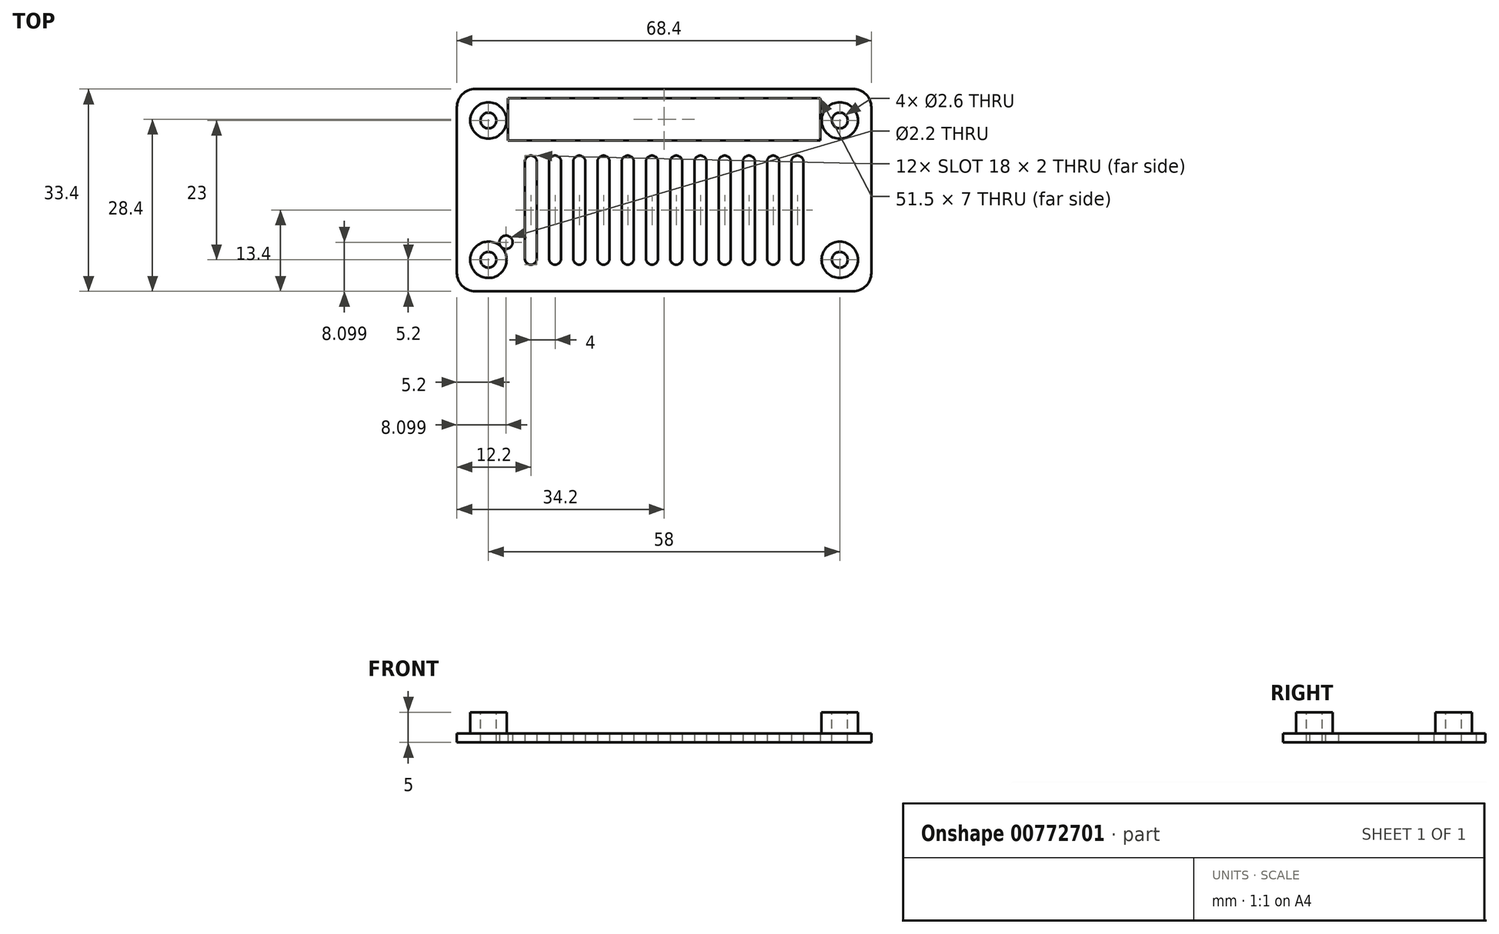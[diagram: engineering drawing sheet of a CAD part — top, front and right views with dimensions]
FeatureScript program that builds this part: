
annotation { "Feature Type Name" : "Feature", "Feature Type Description" : "" }
export const myFeature = defineFeature(function(context is Context, id is Id, definition is map)
    precondition{}
    {
        {
            var Q0;
            Q0=qCreatedBy(makeId("Top.planeOp"),FACE);
            var sketch = newSketch(context, id + "F0", { "sketchPlane" : qUnion([Q0])});
            skLineSegment(sketch, "E0.bottom", {"start": v(-29.5, 15) * mm, "end": v(29.5, 15) * mm, "construction": true});
            skLineSegment(sketch, "E0.top", {"start": v(-29.5, -15) * mm, "end": v(29.5, -15) * mm, "construction": true});
            skLineSegment(sketch, "E0.left", {"start": v(-32.5, 12) * mm, "end": v(-32.5, -12) * mm, "construction": true});
            skLineSegment(sketch, "E0.right", {"start": v(32.5, 12) * mm, "end": v(32.5, -12) * mm, "construction": true});
            skPoint(sketch, "E1.visualSharp", {"position": v(-32.5, 15) * mm});
            skArc(sketch, "E1.filletArc", {"start": v(-29.5, 15) * mm, "mid": v(-31.62, 14.12) * mm, "end": v(-32.5, 12) * mm, "construction": true});
            skPoint(sketch, "E2.visualSharp", {"position": v(32.5, 15) * mm});
            skArc(sketch, "E2.filletArc", {"start": v(32.5, 12) * mm, "mid": v(31.62, 14.12) * mm, "end": v(29.5, 15) * mm, "construction": true});
            skPoint(sketch, "E3.visualSharp", {"position": v(32.5, -15) * mm});
            skArc(sketch, "E3.filletArc", {"start": v(29.5, -15) * mm, "mid": v(31.62, -14.12) * mm, "end": v(32.5, -12) * mm, "construction": true});
            skPoint(sketch, "E4.visualSharp", {"position": v(-32.5, -15) * mm});
            skArc(sketch, "E4.filletArc", {"start": v(-32.5, -12) * mm, "mid": v(-31.62, -14.12) * mm, "end": v(-29.5, -15) * mm, "construction": true});
            skCircle(sketch, "E5", {"center": v(-29, 11.5) * mm, "radius": 3 * mm});
            skCircle(sketch, "E6.0.1.0", {"center": v(-29, -11.5) * mm, "radius": 3 * mm});
            skCircle(sketch, "E6.1.0.0", {"center": v(29, 11.5) * mm, "radius": 3 * mm});
            skCircle(sketch, "E6.1.1.0", {"center": v(29, -11.5) * mm, "radius": 3 * mm});
            skLineSegment(sketch, "E6.direction1", {"start": v(-29, 11.5) * mm, "end": v(29, 11.5) * mm, "construction": true});
            skLineSegment(sketch, "E6.direction2", {"start": v(-29, 11.5) * mm, "end": v(-29, -11.5) * mm, "construction": true});
            skCircle(sketch, "E7", {"center": v(-29, 11.5) * mm, "radius": 1.3 * mm});
            skCircle(sketch, "E8.0.1.0", {"center": v(-29, -11.5) * mm, "radius": 1.3 * mm});
            skCircle(sketch, "E8.1.0.0", {"center": v(29, 11.5) * mm, "radius": 1.3 * mm});
            skCircle(sketch, "E8.1.1.0", {"center": v(29, -11.5) * mm, "radius": 1.3 * mm});
            skLineSegment(sketch, "E9.bottom", {"start": v(-29.7, 15.2) * mm, "end": v(29.7, 15.2) * mm});
            skLineSegment(sketch, "E9.top", {"start": v(-29.7, -15.2) * mm, "end": v(29.7, -15.2) * mm});
            skLineSegment(sketch, "E9.left", {"start": v(-32.7, 12.2) * mm, "end": v(-32.7, -12.2) * mm});
            skLineSegment(sketch, "E9.right", {"start": v(32.7, 12.2) * mm, "end": v(32.7, -12.2) * mm});
            skPoint(sketch, "E10.visualSharp", {"position": v(-32.7, 15.2) * mm});
            skArc(sketch, "E10.filletArc", {"start": v(-29.7, 15.2) * mm, "mid": v(-31.82, 14.32) * mm, "end": v(-32.7, 12.2) * mm});
            skPoint(sketch, "E11.visualSharp", {"position": v(-32.7, -15.2) * mm});
            skArc(sketch, "E11.filletArc", {"start": v(-32.7, -12.2) * mm, "mid": v(-31.82, -14.32) * mm, "end": v(-29.7, -15.2) * mm});
            skPoint(sketch, "E12.visualSharp", {"position": v(32.7, -15.2) * mm});
            skArc(sketch, "E12.filletArc", {"start": v(29.7, -15.2) * mm, "mid": v(31.82, -14.32) * mm, "end": v(32.7, -12.2) * mm});
            skPoint(sketch, "E13.visualSharp", {"position": v(32.7, 15.2) * mm});
            skArc(sketch, "E13.filletArc", {"start": v(32.7, 12.2) * mm, "mid": v(31.82, 14.32) * mm, "end": v(29.7, 15.2) * mm});
            skLineSegment(sketch, "E14.bottom", {"start": v(-31.2, 16.7) * mm, "end": v(31.2, 16.7) * mm});
            skLineSegment(sketch, "E14.top", {"start": v(-31.2, -16.7) * mm, "end": v(31.2, -16.7) * mm});
            skLineSegment(sketch, "E14.left", {"start": v(-34.2, 13.7) * mm, "end": v(-34.2, -13.7) * mm});
            skLineSegment(sketch, "E14.right", {"start": v(34.2, 13.7) * mm, "end": v(34.2, -13.7) * mm});
            skPoint(sketch, "E15.visualSharp", {"position": v(-34.2, 16.7) * mm});
            skArc(sketch, "E15.filletArc", {"start": v(-31.2, 16.7) * mm, "mid": v(-33.32, 15.82) * mm, "end": v(-34.2, 13.7) * mm});
            skPoint(sketch, "E16.visualSharp", {"position": v(-34.2, -16.7) * mm});
            skArc(sketch, "E16.filletArc", {"start": v(-34.2, -13.7) * mm, "mid": v(-33.32, -15.82) * mm, "end": v(-31.2, -16.7) * mm});
            skPoint(sketch, "E17.visualSharp", {"position": v(34.2, -16.7) * mm});
            skArc(sketch, "E17.filletArc", {"start": v(31.2, -16.7) * mm, "mid": v(33.32, -15.82) * mm, "end": v(34.2, -13.7) * mm});
            skPoint(sketch, "E18.visualSharp", {"position": v(34.2, 16.7) * mm});
            skArc(sketch, "E18.filletArc", {"start": v(34.2, 13.7) * mm, "mid": v(33.32, 15.82) * mm, "end": v(31.2, 16.7) * mm});
            skLineSegment(sketch, "E19", {"start": v(0, 33.87) * mm, "end": v(0, -27.8) * mm, "construction": true});
            skLineSegment(sketch, "E20", {"start": v(-38.82, 0) * mm, "end": v(42.98, 0) * mm, "construction": true});
            skSolve(sketch);
        }
        {
            var Q0;
            Q0 = qSketchRegion(id + "F0", true);
            var Q1;
            Q1=makeQuery(id+"F0.imprint","IMPRINT",FACE,{"disambiguationData":[TD([[makeQuery(id+"F0.imprint","IMPRINT",EDGE,{"derivedFrom":sQuery(id+"F0.wireOp",EDGE,"E5")}),-1.0]])]});
            var Q2;
            Q2=makeQuery(id+"F0.imprint","IMPRINT",FACE,{"disambiguationData":[TD([[makeQuery(id+"F0.imprint","IMPRINT",EDGE,{"derivedFrom":sQuery(id+"F0.wireOp",EDGE,"E5")}),1.0]])]});
            var Q3;
            Q3=makeQuery(id+"F0.imprint","IMPRINT",FACE,{"disambiguationData":[TD([[makeQuery(id+"F0.imprint","IMPRINT",EDGE,{"derivedFrom":sQuery(id+"F0.wireOp",EDGE,"E6.0.1.0")}),1.0]])]});
            var Q4;
            Q4=makeQuery(id+"F0.imprint","IMPRINT",FACE,{"disambiguationData":[TD([[makeQuery(id+"F0.imprint","IMPRINT",EDGE,{"derivedFrom":sQuery(id+"F0.wireOp",EDGE,"E6.1.1.0")}),1.0]])]});
            var Q5;
            Q5=makeQuery(id+"F0.imprint","IMPRINT",FACE,{"disambiguationData":[TD([[makeQuery(id+"F0.imprint","IMPRINT",EDGE,{"derivedFrom":sQuery(id+"F0.wireOp",EDGE,"E6.1.0.0")}),1.0]])]});
            extrude(context, id + "F1", {"entities" : qUnion([Q0, Q1, Q2, Q3, Q4, Q5]), "oppositeDirection" : true, "depth" : 1.5 * mm, "offsetDistance" : 25 * mm});
        }
        {
            var Q0;
            Q0=makeQuery(id+"F0.imprint","IMPRINT",FACE,{"disambiguationData":[TD([[makeQuery(id+"F0.imprint","IMPRINT",EDGE,{"derivedFrom":sQuery(id+"F0.wireOp",EDGE,"E5")}),1.0]])]});
            var Q1;
            Q1=makeQuery(id+"F0.imprint","IMPRINT",FACE,{"disambiguationData":[TD([[makeQuery(id+"F0.imprint","IMPRINT",EDGE,{"derivedFrom":sQuery(id+"F0.wireOp",EDGE,"E6.0.1.0")}),1.0]])]});
            var Q2;
            Q2=makeQuery(id+"F0.imprint","IMPRINT",FACE,{"disambiguationData":[TD([[makeQuery(id+"F0.imprint","IMPRINT",EDGE,{"derivedFrom":sQuery(id+"F0.wireOp",EDGE,"E6.1.1.0")}),1.0]])]});
            var Q3;
            Q3=makeQuery(id+"F0.imprint","IMPRINT",FACE,{"disambiguationData":[TD([[makeQuery(id+"F0.imprint","IMPRINT",EDGE,{"derivedFrom":sQuery(id+"F0.wireOp",EDGE,"E6.1.0.0")}),1.0]])]});
            extrude(context, id + "F2", {"entities" : qUnion([Q0, Q1, Q2, Q3]), "operationType" : NewBodyOperationType.ADD, "depth" : 3.5 * mm, "offsetDistance" : 25 * mm});
        }
        {
            var Q0;
            Q0=makeQuery(id+"F1.opExtrude","CAP_FACE",FACE,{"disambiguationData":[OSD([sQuery(id+"F0.wireOp",EDGE,"E7"),sQuery(id+"F0.wireOp",EDGE,"E8.0.1.0"),sQuery(id+"F0.wireOp",EDGE,"E8.1.0.0"),sQuery(id+"F0.wireOp",EDGE,"E8.1.1.0"),sQuery(id+"F0.wireOp",EDGE,"E14.bottom"),sQuery(id+"F0.wireOp",EDGE,"E14.top"),sQuery(id+"F0.wireOp",EDGE,"E14.left"),sQuery(id+"F0.wireOp",EDGE,"E14.right"),sQuery(id+"F0.wireOp",EDGE,"E15.filletArc"),sQuery(id+"F0.wireOp",EDGE,"E16.filletArc"),sQuery(id+"F0.wireOp",EDGE,"E17.filletArc"),sQuery(id+"F0.wireOp",EDGE,"E18.filletArc")])],"isStart":false});
            var sketch = newSketch(context, id + "F3", { "sketchPlane" : qUnion([Q0])});
            skLineSegment(sketch, "E21.0", {"start": v(-29.7, -15.2) * mm, "end": v(29.7, -15.2) * mm, "construction": true});
            skLineSegment(sketch, "E22.0", {"start": v(0, -33.87) * mm, "end": v(0, 27.8) * mm, "construction": true});
            skLineSegment(sketch, "E23.bottom", {"start": v(-25.75, -15.2) * mm, "end": v(25.75, -15.2) * mm});
            skLineSegment(sketch, "E23.top", {"start": v(-25.75, -8.2) * mm, "end": v(25.75, -8.2) * mm});
            skLineSegment(sketch, "E23.left", {"start": v(-25.75, -15.2) * mm, "end": v(-25.75, -8.2) * mm});
            skLineSegment(sketch, "E23.right", {"start": v(25.75, -15.2) * mm, "end": v(25.75, -8.2) * mm});
            skLineSegment(sketch, "E24.bottom", {"start": v(-22, 12.3) * mm, "end": v(-22, 12.3) * mm});
            skLineSegment(sketch, "E24.top", {"start": v(-22, -5.7) * mm, "end": v(-22, -5.7) * mm});
            skLineSegment(sketch, "E24.left", {"start": v(-23, 11.3) * mm, "end": v(-23, -4.7) * mm});
            skLineSegment(sketch, "E24.right", {"start": v(-21, 11.3) * mm, "end": v(-21, -4.7) * mm});
            skPoint(sketch, "E25.visualSharp", {"position": v(-23, 12.3) * mm});
            skArc(sketch, "E25.filletArc", {"start": v(-22, 12.3) * mm, "mid": v(-22.7, 12) * mm, "end": v(-23, 11.3) * mm});
            skPoint(sketch, "E26.visualSharp", {"position": v(-21, 12.3) * mm});
            skArc(sketch, "E26.filletArc", {"start": v(-21, 11.3) * mm, "mid": v(-21.3, 12) * mm, "end": v(-22, 12.3) * mm});
            skPoint(sketch, "E27.visualSharp", {"position": v(-23, -5.7) * mm});
            skArc(sketch, "E27.filletArc", {"start": v(-23, -4.7) * mm, "mid": v(-22.7, -5.4) * mm, "end": v(-22, -5.7) * mm});
            skPoint(sketch, "E28.visualSharp", {"position": v(-21, -5.7) * mm});
            skArc(sketch, "E28.filletArc", {"start": v(-22, -5.7) * mm, "mid": v(-21.3, -5.4) * mm, "end": v(-21, -4.7) * mm});
            skLineSegment(sketch, "E29.1.0.0", {"start": v(-19, 11.3) * mm, "end": v(-19, -4.7) * mm});
            skArc(sketch, "E29.1.0.1", {"start": v(-18, 12.3) * mm, "mid": v(-18.7, 12) * mm, "end": v(-19, 11.3) * mm});
            skArc(sketch, "E29.1.0.2", {"start": v(-17, 11.3) * mm, "mid": v(-17.3, 12) * mm, "end": v(-18, 12.3) * mm});
            skLineSegment(sketch, "E29.1.0.3", {"start": v(-17, 11.3) * mm, "end": v(-17, -4.7) * mm});
            skArc(sketch, "E29.1.0.4", {"start": v(-18, -5.7) * mm, "mid": v(-17.3, -5.4) * mm, "end": v(-17, -4.7) * mm});
            skArc(sketch, "E29.1.0.5", {"start": v(-19, -4.7) * mm, "mid": v(-18.7, -5.4) * mm, "end": v(-18, -5.7) * mm});
            skLineSegment(sketch, "E29.2.0.0", {"start": v(-15, 11.3) * mm, "end": v(-15, -4.7) * mm});
            skArc(sketch, "E29.2.0.1", {"start": v(-14, 12.3) * mm, "mid": v(-14.7, 12) * mm, "end": v(-15, 11.3) * mm});
            skArc(sketch, "E29.2.0.2", {"start": v(-13, 11.3) * mm, "mid": v(-13.3, 12) * mm, "end": v(-14, 12.3) * mm});
            skLineSegment(sketch, "E29.2.0.3", {"start": v(-13, 11.3) * mm, "end": v(-13, -4.7) * mm});
            skArc(sketch, "E29.2.0.4", {"start": v(-14, -5.7) * mm, "mid": v(-13.3, -5.4) * mm, "end": v(-13, -4.7) * mm});
            skArc(sketch, "E29.2.0.5", {"start": v(-15, -4.7) * mm, "mid": v(-14.7, -5.4) * mm, "end": v(-14, -5.7) * mm});
            skLineSegment(sketch, "E29.3.0.0", {"start": v(-11, 11.3) * mm, "end": v(-11, -4.7) * mm});
            skArc(sketch, "E29.3.0.1", {"start": v(-10, 12.3) * mm, "mid": v(-10.7, 12) * mm, "end": v(-11, 11.3) * mm});
            skArc(sketch, "E29.3.0.2", {"start": v(-9, 11.3) * mm, "mid": v(-9.3, 12) * mm, "end": v(-10, 12.3) * mm});
            skLineSegment(sketch, "E29.3.0.3", {"start": v(-9, 11.3) * mm, "end": v(-9, -4.7) * mm});
            skArc(sketch, "E29.3.0.4", {"start": v(-10, -5.7) * mm, "mid": v(-9.3, -5.4) * mm, "end": v(-9, -4.7) * mm});
            skArc(sketch, "E29.3.0.5", {"start": v(-11, -4.7) * mm, "mid": v(-10.7, -5.4) * mm, "end": v(-10, -5.7) * mm});
            skLineSegment(sketch, "E29.4.0.0", {"start": v(-7, 11.3) * mm, "end": v(-7, -4.7) * mm});
            skArc(sketch, "E29.4.0.1", {"start": v(-6, 12.3) * mm, "mid": v(-6.7, 12) * mm, "end": v(-7, 11.3) * mm});
            skArc(sketch, "E29.4.0.2", {"start": v(-5, 11.3) * mm, "mid": v(-5.3, 12) * mm, "end": v(-6, 12.3) * mm});
            skLineSegment(sketch, "E29.4.0.3", {"start": v(-5, 11.3) * mm, "end": v(-5, -4.7) * mm});
            skArc(sketch, "E29.4.0.4", {"start": v(-6, -5.7) * mm, "mid": v(-5.3, -5.4) * mm, "end": v(-5, -4.7) * mm});
            skArc(sketch, "E29.4.0.5", {"start": v(-7, -4.7) * mm, "mid": v(-6.7, -5.4) * mm, "end": v(-6, -5.7) * mm});
            skLineSegment(sketch, "E29.5.0.0", {"start": v(-3, 11.3) * mm, "end": v(-3, -4.7) * mm});
            skArc(sketch, "E29.5.0.1", {"start": v(-2, 12.3) * mm, "mid": v(-2.7, 12) * mm, "end": v(-3, 11.3) * mm});
            skArc(sketch, "E29.5.0.2", {"start": v(-1, 11.3) * mm, "mid": v(-1.3, 12) * mm, "end": v(-2, 12.3) * mm});
            skLineSegment(sketch, "E29.5.0.3", {"start": v(-1, 11.3) * mm, "end": v(-1, -4.7) * mm});
            skArc(sketch, "E29.5.0.4", {"start": v(-2, -5.7) * mm, "mid": v(-1.3, -5.4) * mm, "end": v(-1, -4.7) * mm});
            skArc(sketch, "E29.5.0.5", {"start": v(-3, -4.7) * mm, "mid": v(-2.7, -5.4) * mm, "end": v(-2, -5.7) * mm});
            skLineSegment(sketch, "E29.6.0.0", {"start": v(1, 11.3) * mm, "end": v(1, -4.7) * mm});
            skArc(sketch, "E29.6.0.1", {"start": v(2, 12.3) * mm, "mid": v(1.3, 12) * mm, "end": v(1, 11.3) * mm});
            skArc(sketch, "E29.6.0.2", {"start": v(3, 11.3) * mm, "mid": v(2.7, 12) * mm, "end": v(2, 12.3) * mm});
            skLineSegment(sketch, "E29.6.0.3", {"start": v(3, 11.3) * mm, "end": v(3, -4.7) * mm});
            skArc(sketch, "E29.6.0.4", {"start": v(2, -5.7) * mm, "mid": v(2.7, -5.4) * mm, "end": v(3, -4.7) * mm});
            skArc(sketch, "E29.6.0.5", {"start": v(1, -4.7) * mm, "mid": v(1.3, -5.4) * mm, "end": v(2, -5.7) * mm});
            skLineSegment(sketch, "E29.7.0.0", {"start": v(5, 11.3) * mm, "end": v(5, -4.7) * mm});
            skArc(sketch, "E29.7.0.1", {"start": v(6, 12.3) * mm, "mid": v(5.3, 12) * mm, "end": v(5, 11.3) * mm});
            skArc(sketch, "E29.7.0.2", {"start": v(7, 11.3) * mm, "mid": v(6.7, 12) * mm, "end": v(6, 12.3) * mm});
            skLineSegment(sketch, "E29.7.0.3", {"start": v(7, 11.3) * mm, "end": v(7, -4.7) * mm});
            skArc(sketch, "E29.7.0.4", {"start": v(6, -5.7) * mm, "mid": v(6.7, -5.4) * mm, "end": v(7, -4.7) * mm});
            skArc(sketch, "E29.7.0.5", {"start": v(5, -4.7) * mm, "mid": v(5.3, -5.4) * mm, "end": v(6, -5.7) * mm});
            skLineSegment(sketch, "E29.8.0.0", {"start": v(9, 11.3) * mm, "end": v(9, -4.7) * mm});
            skArc(sketch, "E29.8.0.1", {"start": v(10, 12.3) * mm, "mid": v(9.3, 12) * mm, "end": v(9, 11.3) * mm});
            skArc(sketch, "E29.8.0.2", {"start": v(11, 11.3) * mm, "mid": v(10.7, 12) * mm, "end": v(10, 12.3) * mm});
            skLineSegment(sketch, "E29.8.0.3", {"start": v(11, 11.3) * mm, "end": v(11, -4.7) * mm});
            skArc(sketch, "E29.8.0.4", {"start": v(10, -5.7) * mm, "mid": v(10.7, -5.4) * mm, "end": v(11, -4.7) * mm});
            skArc(sketch, "E29.8.0.5", {"start": v(9, -4.7) * mm, "mid": v(9.3, -5.4) * mm, "end": v(10, -5.7) * mm});
            skLineSegment(sketch, "E29.9.0.0", {"start": v(13, 11.3) * mm, "end": v(13, -4.7) * mm});
            skArc(sketch, "E29.9.0.1", {"start": v(14, 12.3) * mm, "mid": v(13.3, 12) * mm, "end": v(13, 11.3) * mm});
            skArc(sketch, "E29.9.0.2", {"start": v(15, 11.3) * mm, "mid": v(14.7, 12) * mm, "end": v(14, 12.3) * mm});
            skLineSegment(sketch, "E29.9.0.3", {"start": v(15, 11.3) * mm, "end": v(15, -4.7) * mm});
            skArc(sketch, "E29.9.0.4", {"start": v(14, -5.7) * mm, "mid": v(14.7, -5.4) * mm, "end": v(15, -4.7) * mm});
            skArc(sketch, "E29.9.0.5", {"start": v(13, -4.7) * mm, "mid": v(13.3, -5.4) * mm, "end": v(14, -5.7) * mm});
            skLineSegment(sketch, "E29.10.0.0", {"start": v(17, 11.3) * mm, "end": v(17, -4.7) * mm});
            skArc(sketch, "E29.10.0.1", {"start": v(18, 12.3) * mm, "mid": v(17.3, 12) * mm, "end": v(17, 11.3) * mm});
            skArc(sketch, "E29.10.0.2", {"start": v(19, 11.3) * mm, "mid": v(18.7, 12) * mm, "end": v(18, 12.3) * mm});
            skLineSegment(sketch, "E29.10.0.3", {"start": v(19, 11.3) * mm, "end": v(19, -4.7) * mm});
            skArc(sketch, "E29.10.0.4", {"start": v(18, -5.7) * mm, "mid": v(18.7, -5.4) * mm, "end": v(19, -4.7) * mm});
            skArc(sketch, "E29.10.0.5", {"start": v(17, -4.7) * mm, "mid": v(17.3, -5.4) * mm, "end": v(18, -5.7) * mm});
            skLineSegment(sketch, "E29.11.0.0", {"start": v(21, 11.3) * mm, "end": v(21, -4.7) * mm});
            skArc(sketch, "E29.11.0.1", {"start": v(22, 12.3) * mm, "mid": v(21.3, 12) * mm, "end": v(21, 11.3) * mm});
            skArc(sketch, "E29.11.0.2", {"start": v(23, 11.3) * mm, "mid": v(22.7, 12) * mm, "end": v(22, 12.3) * mm});
            skLineSegment(sketch, "E29.11.0.3", {"start": v(23, 11.3) * mm, "end": v(23, -4.7) * mm});
            skArc(sketch, "E29.11.0.4", {"start": v(22, -5.7) * mm, "mid": v(22.7, -5.4) * mm, "end": v(23, -4.7) * mm});
            skArc(sketch, "E29.11.0.5", {"start": v(21, -4.7) * mm, "mid": v(21.3, -5.4) * mm, "end": v(22, -5.7) * mm});
            skLineSegment(sketch, "E29.direction1", {"start": v(-22, -5.7) * mm, "end": v(-18, -5.7) * mm, "construction": true});
            skSolve(sketch);
        }
        {
            var Q0;
            Q0 = qSketchRegion(id + "F3", true);
            extrude(context, id + "F4", {"entities" : qUnion([Q0]), "operationType" : NewBodyOperationType.REMOVE, "oppositeDirection" : true, "depth" : 25 * mm, "offsetDistance" : 25 * mm});
        }
        {
            var Q0;
            Q0=makeQuery(id+"F1.opExtrude","CAP_FACE",FACE,{"disambiguationData":[OSD([sQuery(id+"F0.wireOp",EDGE,"E7"),sQuery(id+"F0.wireOp",EDGE,"E8.0.1.0"),sQuery(id+"F0.wireOp",EDGE,"E8.1.0.0"),sQuery(id+"F0.wireOp",EDGE,"E8.1.1.0"),sQuery(id+"F0.wireOp",EDGE,"E14.bottom"),sQuery(id+"F0.wireOp",EDGE,"E14.top"),sQuery(id+"F0.wireOp",EDGE,"E14.left"),sQuery(id+"F0.wireOp",EDGE,"E14.right"),sQuery(id+"F0.wireOp",EDGE,"E15.filletArc"),sQuery(id+"F0.wireOp",EDGE,"E16.filletArc"),sQuery(id+"F0.wireOp",EDGE,"E17.filletArc"),sQuery(id+"F0.wireOp",EDGE,"E18.filletArc")])],"isStart":false});
            var sketch = newSketch(context, id + "F5", { "sketchPlane" : qUnion([Q0])});
            skCircle(sketch, "E30.0", {"center": v(-29, 11.5) * mm, "radius": 3 * mm, "construction": true});
            skCircle(sketch, "E31", {"center": v(-26.1, 8.6) * mm, "radius": 1.1 * mm});
            skLineSegment(sketch, "E32", {"start": v(-26.1, 8.6) * mm, "end": v(-29, 11.5) * mm, "construction": true});
            skSolve(sketch);
        }
        {
            var Q0;
            Q0=makeQuery(id+"F5.imprint","IMPRINT",FACE,{"disambiguationData":[TD([[makeQuery(id+"F5.imprint","IMPRINT",EDGE,{"derivedFrom":sQuery(id+"F5.wireOp",EDGE,"E31")}),1.0]])]});
            extrude(context, id + "F6", {"entities" : qUnion([Q0]), "operationType" : NewBodyOperationType.REMOVE, "oppositeDirection" : true, "depth" : 25 * mm, "offsetDistance" : 25 * mm});
        }
    });
